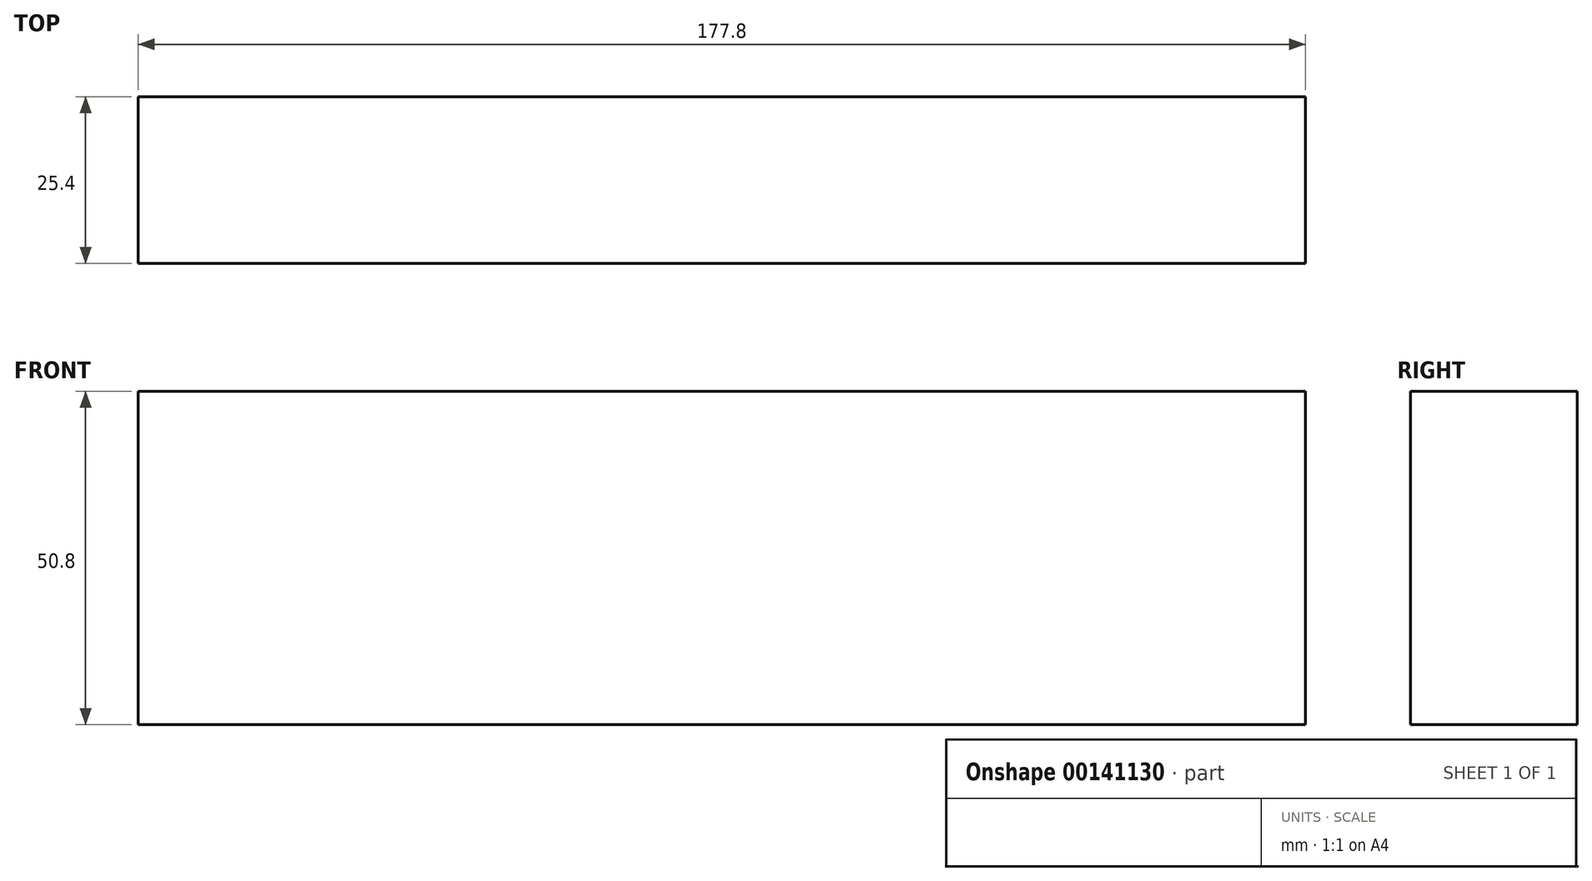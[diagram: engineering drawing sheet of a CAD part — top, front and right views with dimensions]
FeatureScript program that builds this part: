
annotation { "Feature Type Name" : "Feature", "Feature Type Description" : "" }
export const myFeature = defineFeature(function(context is Context, id is Id, definition is map)
    precondition{}
    {
        {
            var Q0;
            Q0=qCreatedBy(makeId("Front.planeOp"),FACE);
            var sketch = newSketch(context, id + "F0", { "sketchPlane" : qUnion([Q0])});
            skLineSegment(sketch, "E0.bottom", {"start": v(0, 0) * mm, "end": v(177.8, 0) * mm});
            skLineSegment(sketch, "E0.top", {"start": v(0, 50.8) * mm, "end": v(177.8, 50.8) * mm});
            skLineSegment(sketch, "E0.left", {"start": v(0, 0) * mm, "end": v(0, 50.8) * mm});
            skLineSegment(sketch, "E0.right", {"start": v(177.8, 0) * mm, "end": v(177.8, 50.8) * mm});
            skSolve(sketch);
        }
        {
            var Q0;
            Q0 = qSketchRegion(id + "F0", true);
            extrude(context, id + "F1", {"entities" : qUnion([Q0]), "depth" : 25.4 * mm});
        }
    });
